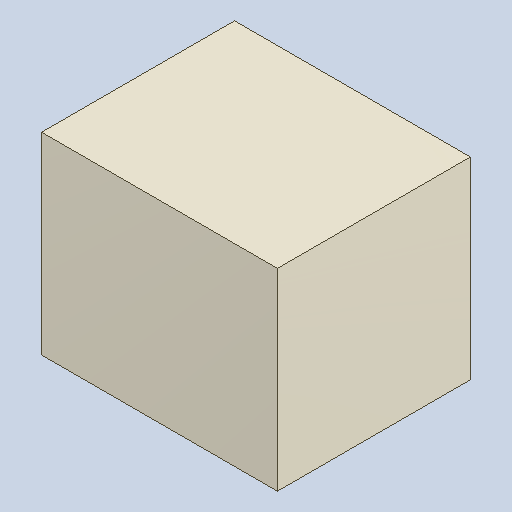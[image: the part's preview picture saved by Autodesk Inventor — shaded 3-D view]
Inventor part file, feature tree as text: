
AUTODESK INVENTOR PART (.ipt)
format: ipt  version: 2023.4 (Build 274418000, 418)  size: 81,920 bytes
history: native  units: mm
features: extrude x1
ambient origin geometry x8: Origin, YZ Plane, XZ Plane, XY Plane, X Axis, Y Axis, Z Axis, Center Point
bodies: Solid1 (feature_tree)
feature tree (1):
  extrude  "Extruded_22"  [1 undecoded]
note: 1 required parameter value undecoded (feature->parameter linkage not recoverable at this tier; creation-order binding heuristic only, values carry confidence <= 0.55)
